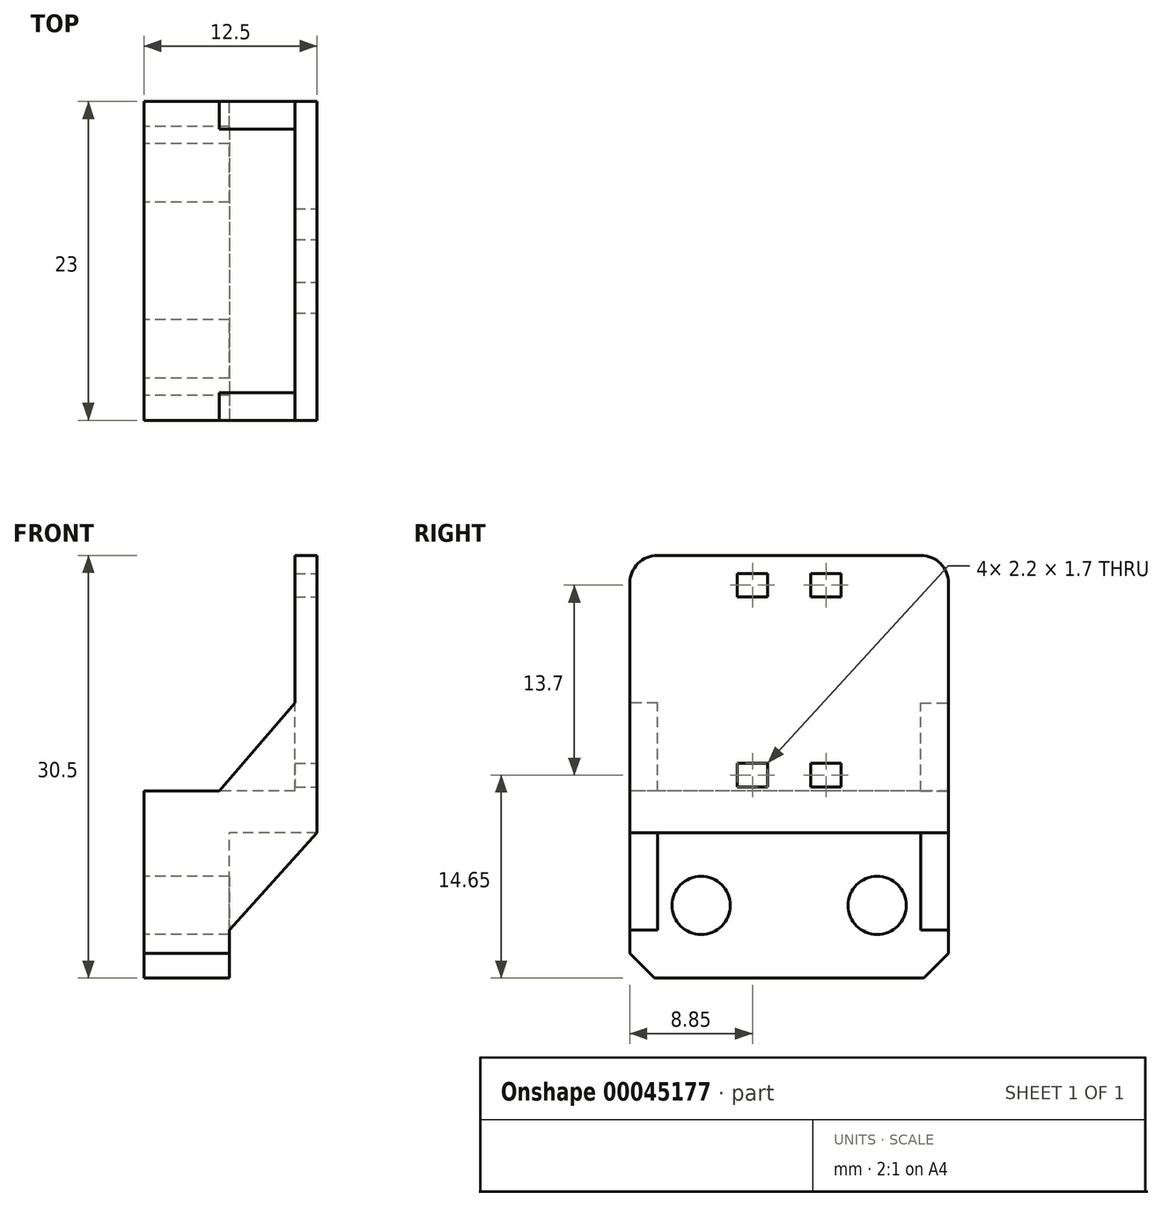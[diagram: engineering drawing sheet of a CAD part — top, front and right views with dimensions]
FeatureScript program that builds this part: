
annotation { "Feature Type Name" : "Feature", "Feature Type Description" : "" }
export const myFeature = defineFeature(function(context is Context, id is Id, definition is map)
    precondition{}
    {
        {
            var Q0;
            Q0=qCreatedBy(makeId("Right.planeOp"),FACE);
            var sketch = newSketch(context, id + "F0", { "sketchPlane" : qUnion([Q0])});
            skLineSegment(sketch, "E0.rect.bottom", {"start": v(9.71, -5.25) * mm, "end": v(-9.71, -5.25) * mm});
            skLineSegment(sketch, "E0.rect.top", {"start": v(9.71, 5.25) * mm, "end": v(-9.71, 5.25) * mm});
            skLineSegment(sketch, "E0.rect.left", {"start": v(11.5, -3.46) * mm, "end": v(11.5, 3.46) * mm});
            skLineSegment(sketch, "E0.rect.right", {"start": v(-11.5, -3.46) * mm, "end": v(-11.5, 3.46) * mm});
            skPoint(sketch, "E0.rect.middle", {"position": v(0, 0) * mm});
            skLineSegment(sketch, "E1", {"start": v(6.35, 5.25) * mm, "end": v(6.35, -5.25) * mm, "construction": true});
            skCircle(sketch, "E2", {"center": v(6.35, 0) * mm, "radius": 2.1 * mm});
            skCircle(sketch, "E3.MirrorC", {"center": v(-6.35, 0) * mm, "radius": 2.1 * mm});
            skLineSegment(sketch, "E4.MirrorCS", {"start": v(-9.71, -5.25) * mm, "end": v(-11.5, -3.46) * mm});
            skLineSegment(sketch, "E5.MirrorCS", {"start": v(9.71, -5.25) * mm, "end": v(11.5, -3.46) * mm});
            skPoint(sketch, "E6.orphan", {"position": v(-11.5, 5.25) * mm});
            skPoint(sketch, "E7.orphan", {"position": v(-11.5, -5.25) * mm});
            skPoint(sketch, "E8.orphan", {"position": v(11.5, 5.25) * mm});
            skPoint(sketch, "E9.orphan", {"position": v(11.5, -5.25) * mm});
            skLineSegment(sketch, "E10", {"start": v(11.5, 3.46) * mm, "end": v(11.5, 5.25) * mm});
            skLineSegment(sketch, "E11", {"start": v(11.5, 5.25) * mm, "end": v(9.71, 5.25) * mm});
            skLineSegment(sketch, "E12", {"start": v(-11.5, 3.46) * mm, "end": v(-11.5, 5.25) * mm});
            skLineSegment(sketch, "E13", {"start": v(-11.5, 5.25) * mm, "end": v(-9.71, 5.25) * mm});
            skSolve(sketch);
        }
        {
            var Q0;
            Q0=makeQuery(id+"F0.imprint","IMPRINT",FACE,{"disambiguationData":[TD([[makeQuery(id+"F0.imprint","IMPRINT",EDGE,{"derivedFrom":sQuery(id+"F0.wireOp",EDGE,"E0.rect.bottom")}),-1.0]])]});
            extrude(context, id + "F1", {"entities" : qUnion([Q0]), "depth" : 6.16 * mm});
        }
        {
            var Q0;
            Q0=makeQuery(id+"F1.opExtrude","CAP_FACE",FACE,{"disambiguationData":[OSD([sQuery(id+"F0.wireOp",EDGE,"E0.rect.bottom"),sQuery(id+"F0.wireOp",EDGE,"E0.rect.top"),sQuery(id+"F0.wireOp",EDGE,"E0.rect.left"),sQuery(id+"F0.wireOp",EDGE,"E0.rect.right"),sQuery(id+"F0.wireOp",EDGE,"E2"),sQuery(id+"F0.wireOp",EDGE,"E3.MirrorC"),sQuery(id+"F0.wireOp",EDGE,"E4.MirrorCS"),sQuery(id+"F0.wireOp",EDGE,"E5.MirrorCS"),sQuery(id+"F0.wireOp",EDGE,"E10"),sQuery(id+"F0.wireOp",EDGE,"E11"),sQuery(id+"F0.wireOp",EDGE,"E12"),sQuery(id+"F0.wireOp",EDGE,"E13")])],"isStart":true});
            var sketch = newSketch(context, id + "F2", { "sketchPlane" : qUnion([Q0])});
            skLineSegment(sketch, "E14.bottom", {"start": v(-11.5, 5.25) * mm, "end": v(11.5, 5.25) * mm});
            skLineSegment(sketch, "E14.top", {"start": v(-11.5, 8.25) * mm, "end": v(11.5, 8.25) * mm});
            skLineSegment(sketch, "E14.left", {"start": v(-11.5, 5.25) * mm, "end": v(-11.5, 8.25) * mm});
            skLineSegment(sketch, "E14.right", {"start": v(11.5, 5.25) * mm, "end": v(11.5, 8.25) * mm});
            skSolve(sketch);
        }
        {
            var Q0;
            Q0 = qSketchRegion(id + "F2", true);
            extrude(context, id + "F3", {"entities" : qUnion([Q0]), "oppositeDirection" : true, "depth" : 12.5 * mm});
        }
        {
            var Q0;
            Q0=makeQuery(id+"F3.opExtrude","CAP_FACE",FACE,{"disambiguationData":[OSD([sQuery(id+"F2.wireOp",EDGE,"E14.bottom"),sQuery(id+"F2.wireOp",EDGE,"E14.top"),sQuery(id+"F2.wireOp",EDGE,"E14.left"),sQuery(id+"F2.wireOp",EDGE,"E14.right")])],"isStart":false});
            var sketch = newSketch(context, id + "F4", { "sketchPlane" : qUnion([Q0])});
            skLineSegment(sketch, "E15.bottom", {"start": v(-11.5, 5.25) * mm, "end": v(11.5, 5.25) * mm});
            skLineSegment(sketch, "E15.top", {"start": v(-11.5, 25.25) * mm, "end": v(11.5, 25.25) * mm});
            skLineSegment(sketch, "E15.left", {"start": v(-11.5, 5.25) * mm, "end": v(-11.5, 25.25) * mm});
            skLineSegment(sketch, "E15.right", {"start": v(11.5, 5.25) * mm, "end": v(11.5, 25.25) * mm});
            skLineSegment(sketch, "E16", {"start": v(-11.5, 16.25) * mm, "end": v(11.5, 16.25) * mm, "construction": true});
            skLineSegment(sketch, "E17.rect.bottom", {"start": v(3.75, 22.25) * mm, "end": v(-3.75, 22.25) * mm, "construction": true});
            skLineSegment(sketch, "E17.rect.top", {"start": v(3.75, 10.25) * mm, "end": v(-3.75, 10.25) * mm, "construction": true});
            skLineSegment(sketch, "E17.rect.left", {"start": v(3.75, 22.25) * mm, "end": v(3.75, 10.25) * mm, "construction": true});
            skLineSegment(sketch, "E17.rect.right", {"start": v(-3.75, 22.25) * mm, "end": v(-3.75, 10.25) * mm, "construction": true});
            skPoint(sketch, "E17.rect.middle", {"position": v(0, 16.25) * mm});
            skLineSegment(sketch, "E18.bottom", {"start": v(3.75, 22.25) * mm, "end": v(1.55, 22.25) * mm});
            skLineSegment(sketch, "E18.top", {"start": v(3.75, 23.95) * mm, "end": v(1.55, 23.95) * mm});
            skLineSegment(sketch, "E18.left", {"start": v(3.75, 22.25) * mm, "end": v(3.75, 23.95) * mm});
            skLineSegment(sketch, "E18.right", {"start": v(1.55, 22.25) * mm, "end": v(1.55, 23.95) * mm});
            skLineSegment(sketch, "E19.MirrorCS", {"start": v(-3.75, 23.95) * mm, "end": v(-1.55, 23.95) * mm});
            skLineSegment(sketch, "E20.MirrorCS", {"start": v(-1.55, 22.25) * mm, "end": v(-1.55, 23.95) * mm});
            skLineSegment(sketch, "E21.MirrorCS", {"start": v(-3.75, 22.25) * mm, "end": v(-1.55, 22.25) * mm});
            skLineSegment(sketch, "E22.MirrorCS", {"start": v(-3.75, 22.25) * mm, "end": v(-3.75, 23.95) * mm});
            skLineSegment(sketch, "E23.MirrorCS", {"start": v(3.75, 8.55) * mm, "end": v(1.55, 8.55) * mm});
            skLineSegment(sketch, "E24.MirrorCS", {"start": v(1.55, 10.25) * mm, "end": v(1.55, 8.55) * mm});
            skLineSegment(sketch, "E25.MirrorCS", {"start": v(3.75, 10.25) * mm, "end": v(1.55, 10.25) * mm});
            skLineSegment(sketch, "E26.MirrorCS", {"start": v(3.75, 10.25) * mm, "end": v(3.75, 8.55) * mm});
            skLineSegment(sketch, "E27.MirrorCS", {"start": v(-3.75, 8.55) * mm, "end": v(-1.55, 8.55) * mm});
            skLineSegment(sketch, "E28.MirrorCS", {"start": v(-3.75, 10.25) * mm, "end": v(-1.55, 10.25) * mm});
            skLineSegment(sketch, "E29.MirrorCS", {"start": v(-3.75, 10.25) * mm, "end": v(-3.75, 8.55) * mm});
            skLineSegment(sketch, "E30.MirrorCS", {"start": v(-1.55, 10.25) * mm, "end": v(-1.55, 8.55) * mm});
            skSolve(sketch);
        }
        {
            var Q0;
            Q0 = qSketchRegion(id + "F4", true);
            extrude(context, id + "F5", {"entities" : qUnion([Q0]), "operationType" : NewBodyOperationType.ADD, "oppositeDirection" : true, "depth" : 1.6 * mm});
        }
        {
            var Q0;
            Q0=makeQuery(id+"F3.opExtrude","SWEPT_BODY",BODY,{"disambiguationData":[OSD([sQuery(id+"F2.wireOp",EDGE,"E14.bottom"),sQuery(id+"F2.wireOp",EDGE,"E14.top"),sQuery(id+"F2.wireOp",EDGE,"E14.left"),sQuery(id+"F2.wireOp",EDGE,"E14.right")])]});
            var Q1;
            Q1=makeQuery(id+"F1.opExtrude","SWEPT_BODY",BODY,{"disambiguationData":[OSD([sQuery(id+"F0.wireOp",EDGE,"E0.rect.bottom"),sQuery(id+"F0.wireOp",EDGE,"E0.rect.top"),sQuery(id+"F0.wireOp",EDGE,"E0.rect.left"),sQuery(id+"F0.wireOp",EDGE,"E0.rect.right"),sQuery(id+"F0.wireOp",EDGE,"E2"),sQuery(id+"F0.wireOp",EDGE,"E3.MirrorC"),sQuery(id+"F0.wireOp",EDGE,"E4.MirrorCS"),sQuery(id+"F0.wireOp",EDGE,"E5.MirrorCS"),sQuery(id+"F0.wireOp",EDGE,"E10"),sQuery(id+"F0.wireOp",EDGE,"E11"),sQuery(id+"F0.wireOp",EDGE,"E12"),sQuery(id+"F0.wireOp",EDGE,"E13")])]});
            booleanBodies(context, id + "F6", {"operationType" : BooleanOperationType.UNION, "tools" : qUnion([Q0, Q1])});
        }
        {
            var Q0;
            Q0=makeQuery(id+"F6.opBoolean","MERGE",FACE,{"derivedFrom":[makeQuery(id+"F1.opExtrude","SWEPT_FACE",FACE,{"disambiguationData":[OSD([sQuery(id+"F0.wireOp",EDGE,"E0.rect.left"),sQuery(id+"F0.wireOp",EDGE,"E10")])]}),makeQuery(id+"F5.boolean.opBoolean","MERGE",FACE,{"derivedFrom":[makeQuery(id+"F3.opExtrude","SWEPT_FACE",FACE,{"disambiguationData":[OSD([sQuery(id+"F2.wireOp",EDGE,"E14.left")])]}),makeQuery(id+"F5.opExtrude","SWEPT_FACE",FACE,{"disambiguationData":[OSD([sQuery(id+"F4.wireOp",EDGE,"E15.right")])]})]})]});
            var sketch = newSketch(context, id + "F7", { "sketchPlane" : qUnion([Q0])});
            skLineSegment(sketch, "E31", {"start": v(-10.9, 14.6) * mm, "end": v(-5.45, 8.25) * mm});
            skLineSegment(sketch, "E32", {"start": v(-5.45, 8.25) * mm, "end": v(-10.9, 8.25) * mm});
            skLineSegment(sketch, "E33", {"start": v(-10.9, 8.25) * mm, "end": v(-10.9, 14.6) * mm});
            skLineSegment(sketch, "E34", {"start": v(-12.5, 5.25) * mm, "end": v(-6.16, -1.77) * mm});
            skLineSegment(sketch, "E35", {"start": v(-6.16, -1.77) * mm, "end": v(-6.16, 5.25) * mm});
            skLineSegment(sketch, "E36", {"start": v(-6.16, 5.25) * mm, "end": v(-12.5, 5.25) * mm});
            skSolve(sketch);
        }
        {
            var Q0;
            Q0 = qSketchRegion(id + "F7", true);
            extrude(context, id + "F8", {"entities" : qUnion([Q0]), "oppositeDirection" : true, "depth" : 2 * mm});
        }
        {
            var Q0;
            Q0=qCreatedBy(makeId("Front.planeOp"),FACE);
            cPlane(context, id + "F9", {"entities" : qUnion([Q0]), "cplaneType" : CPlaneType.OFFSET, "offset" : 0 * mm, "width" : 150 * mm, "height" : 150 * mm});
        }
        {
            var Q0;
            Q0=makeQuery(id+"F8.opExtrude","SWEPT_BODY",BODY,{"disambiguationData":[OSD([sQuery(id+"F7.wireOp",EDGE,"E31"),sQuery(id+"F7.wireOp",EDGE,"E32"),sQuery(id+"F7.wireOp",EDGE,"E33")])]});
            var Q1;
            Q1=qCreatedBy(id+"F9.planeOp",FACE);
            mirror(context, id + "F10", {"operationType" : NewBodyOperationType.ADD, "entities" : qUnion([Q0]), "mirrorPlane" : qUnion([Q1])});
        }
        {
            var Q0;
            Q0=makeQuery(id+"F8.opExtrude","SWEPT_BODY",BODY,{"disambiguationData":[OSD([sQuery(id+"F7.wireOp",EDGE,"E34"),sQuery(id+"F7.wireOp",EDGE,"E35"),sQuery(id+"F7.wireOp",EDGE,"E36")])]});
            var Q1;
            Q1=qCreatedBy(id+"F9.planeOp",FACE);
            mirror(context, id + "F11", {"operationType" : NewBodyOperationType.ADD, "entities" : qUnion([Q0]), "mirrorPlane" : qUnion([Q1])});
        }
        {
            var Q0;
            Q0=makeQuery(id+"F5.opExtrude","SWEPT_EDGE",EDGE,{"disambiguationData":[OSD([sQuery(id+"F4.wireOp",EDGE,"E15.top"),sQuery(id+"F4.wireOp",EDGE,"E15.right")])]});
            var Q1;
            Q1=makeQuery(id+"F5.opExtrude","SWEPT_EDGE",EDGE,{"disambiguationData":[OSD([sQuery(id+"F4.wireOp",EDGE,"E15.top"),sQuery(id+"F4.wireOp",EDGE,"E15.left")])]});
            fillet(context, id + "F12", {"entities" : qUnion([Q0, Q1]), "radius" : 2 * mm, "tangentPropagation" : true, "allowEdgeOverflow" : false});
        }
    });
